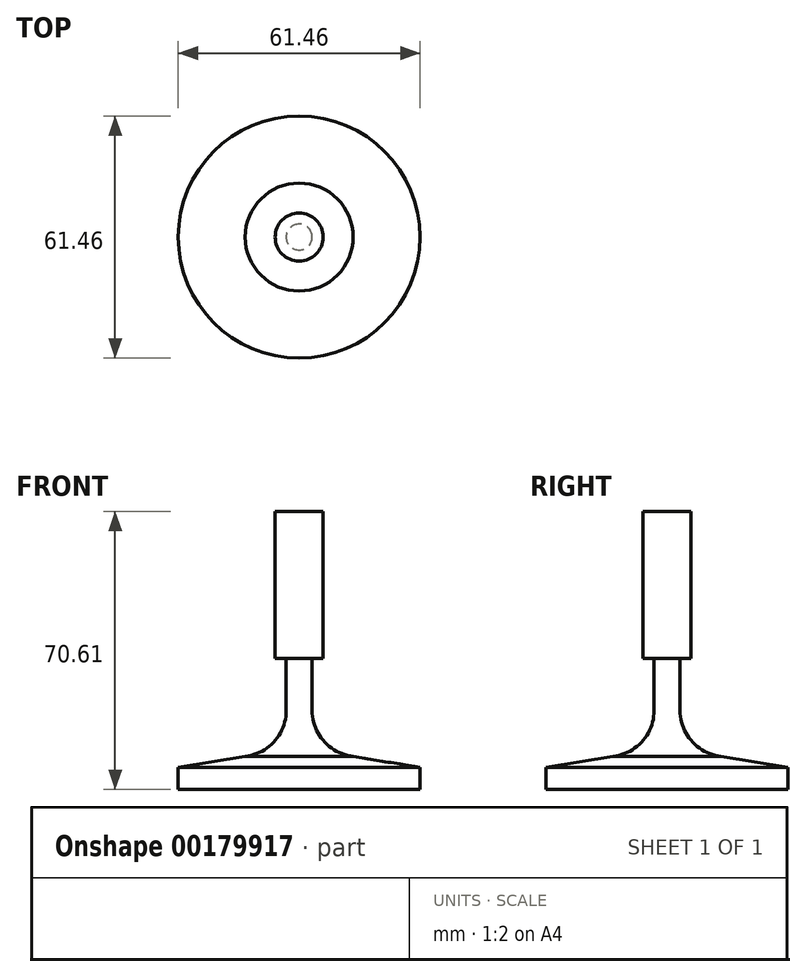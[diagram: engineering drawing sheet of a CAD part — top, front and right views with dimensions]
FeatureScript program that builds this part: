
annotation { "Feature Type Name" : "Feature", "Feature Type Description" : "" }
export const myFeature = defineFeature(function(context is Context, id is Id, definition is map)
    precondition{}
    {
        {
            var Q0;
            Q0=qCreatedBy(makeId("Front.planeOp"),FACE);
            var sketch = newSketch(context, id + "F0", { "sketchPlane" : qUnion([Q0])});
            skLineSegment(sketch, "E0", {"start": v(0, 70.61) * mm, "end": v(0, 0) * mm});
            skLineSegment(sketch, "E1", {"start": v(0, 0) * mm, "end": v(30.73, 0) * mm});
            skLineSegment(sketch, "E2", {"start": v(30.73, 0) * mm, "end": v(30.73, 5.59) * mm});
            skLineSegment(sketch, "E3", {"start": v(30.73, 5.59) * mm, "end": v(13.72, 8.38) * mm});
            skLineSegment(sketch, "E4", {"start": v(0, 70.61) * mm, "end": v(6.1, 70.61) * mm});
            skLineSegment(sketch, "E5", {"start": v(6.1, 70.61) * mm, "end": v(6.1, 33.27) * mm});
            skLineSegment(sketch, "E6", {"start": v(6.1, 33.27) * mm, "end": v(3.3, 33.27) * mm});
            skLineSegment(sketch, "E7", {"start": v(3.3, 33.27) * mm, "end": v(3.3, 20.07) * mm});
            skArc(sketch, "E8", {"start": v(3.3, 20.07) * mm, "mid": v(6.28, 12.24) * mm, "end": v(13.72, 8.38) * mm});
            skSolve(sketch);
        }
        {
            var Q0;
            Q0 = qSketchRegion(id + "F0", true);
            var Q1;
            Q1=sQuery(id+"F0.wireOp",EDGE,"E0");
            revolve(context, id + "F1", {"entities" : qUnion([Q0]), "axis" : qUnion([Q1]), "revolveType" : RevolveType.FULL});
        }
    });
